# Revit family: SIMES_S.1533W_Keen pole mounted
name_source: partatom
category: Lighting Fixtures
revit_build: Autodesk Revit 2016 (Build: 20150714_1515(x64)
units: mm (PartAtom-declared; Revit-internal decimal feet)

## family parameters
Cut with Voids When Loaded = No
Host = Face
Light Source = No
OmniClass Number = 23.80.70.14
OmniClass Title = Luminaries for External Lighting
Part Type = Normal
Room Calculation Point = No
Round Connector Dimension = Use Diameter
Shared = No

## types (1)
- SIMES_S.1533W_Keen pole mounted
    Approval mark = CE, ENEC
    Assembly Code = D5020
    Color Rendering Index = CRI 90
    Colour Temperature = 3000
    Control Gear = electronic transformer
    Default Elevation = 1219 mm
    Description = KEEN POLE MOUNTED
Art. S.1533W
MODULES LED 3000K  230V CRI 90 MacAdam step 3
Rated luminaire luminous flux: 886lm
Rated input power: 16W
Luminaire efficacy: 55lm/W
Electronic ballast 220÷240V 0/50/60Hz
CE - ENEC 03

Fixture available with integral DALI driver on request with surcharge.

PRODUCT TYPE
Projector. IP rating IP 65
MATERIAL CHARACTERISTICS
Die-cast EN AB-47100 aluminium housing with high corrosion resistance.
Stone wash surface treatment prior to painting process. A4 grade Stainless Steel screws with 2,5-3% molybdenum content which increases the resistance against corrosion. Silicone gaskets. Painting Process : 3 Step Process
1) Surface treatment with BONDERITE. A heavy metal free chemical surface treatment containing ceramic nano particles giving a cohesive, inorganic and highly dense protective coating. 2) PRE POLYMERIZATION a process of introducing an epoxy primer with excellent characteristics to the paint which also offers very high resistance to oxidation due to its Zinc content. 3) POLYMERIZATION a process with the application of polyester powder with high resistance against UV rays and harsh weather conditions. Resistance test protection for Marine applications for 1200h.  Mechanical resistance IK 06
LIGHTING PERFORMANCE
The special joint guarantees total freedom in directing the light beam: the luminaire is able to rotate on three different axes. Clear toughened glass. LOR -- 
INSTALLATION AND MAINTENANCE
The tempered front glass diffuser is fixed externally to the fitting through silicon resin, perfectly flush with the front ring. Water and dirt deposits that can disturb the lighting performance of the projector can easily flow away. The special double joint
guarantees total freedom in directing the light beam: the luminaire is able to rotate on three different axes. The pre-wired connecting wall plaquette and its fast connector make the installation and maintenance process quick, easy and safe. Versions for pole installation: Thanks to the special anchor base the luminaire can be fixed to new or existing poles of diameter of no less than 60 mm. Megakeen projector in standard version can be directly fixed to poles of diameter min ø 60 mm and max ø 300 mm without requiring any flange or bracket. Installation is carried out by making two holes (Ø 12 mm) in the pole: one for the fixing screw a one for the supply cable.
WIRING
MICROKEEN supplied with a 1,5m pre-wired H05RN-F  (1,0 MINIKEEN , 0,3m KEEN) cable and fast connector. KEEN e MINIKEEN pole mounted supplied with 6m pre-wired H05RN-F cable. Isolation: CLASS II . Available colours: White (cod.01), Aluminium grey (cod.14). Weight: 2 Kg Glow Wire test: --
L.E.D circuit included.
KEEN PATENTED , REGISTERED DESIGN
This luminaire contains built-in LED modules with energy class: A, A+, A++. In case of damage or malfunction please contact the manufacturer to receive additional instructions on how to replace and relative spare parts to order. The LED modules cannot be handled in the luminaire by the end user (Regulation UE 874/2012).
LED circuit boards are engineered accordingly to actual Lumen Maintenance regulation (LM80) and Technical Memorandum (TM21) where uniformity and quality of light is 50.000 hours referred to L70  B20 Ta 25°C.Lifecycle refers to LED circuit boards only, all others components of the luminaire are excluded.

EMERGENCY VERSIONS The fittings operates both on AC ( 50/60Hz ) and DC ( 0Hz ) voltage.
    Frequency = 0/50/60Hz
    IFC Classification = Light Fixture
    IK Rating = IK 06
    Lamp = LED
    Lamp Light Flux = 1180
    Lamp count = 1
    Last Update = 08/11/2018 09:55:36
    Lifetime = 50000 L70 B20 Ta 25°C
    Light Output Ratio = 100
    Luminous efficacy = 55,4
    Manufacturer = SIMES
    Masterformat 2014 Code = 26 56 00
    Masterformat 2014 Description = Exterior Lighting
    Model = S.1533W
    Mounting Place = Pole
    Mounting Type = Surface mounted
    NBS Reference Code = 49
    NBS Reference Description = Luminaries And Lamps
    OmniClass Code = 23-35 47 11
    OmniClass Description = Lighting Fixture
    Product Group = projector
    Product Name = Keen pole mounted
    Protection Class = Protection class II
    Protection Degree = IP 65
    System Light Flux = 886
    System Power = 16
    Type Comments = SIMES S.p.A. - All rights reserved
    Type Image = keen_da_palo.jpg
    UNSPSC Code = 3911
    URL = http://www.simes.it
    Uniclass 1.4 Code = YJ73
    Uniclass 1.4 Description = Luminaries and lamps
    Uniclass 2.0 Code = PR-49
    Uniclass 2.0 Description = Luminaries and lamps
    Uniclass 2015 Code = EF_70_80
    Uniclass 2015 Name = Lighting
    Uniformat II Code = D5020
    Uniformat II Description = Lighting & Branch Wiring
    Voltage = 220÷240V
    Wattage Comments = 16.0W

## geometry (parser evidence)
native form markers: Blend x2
no freeform markers — native parametric forms only
